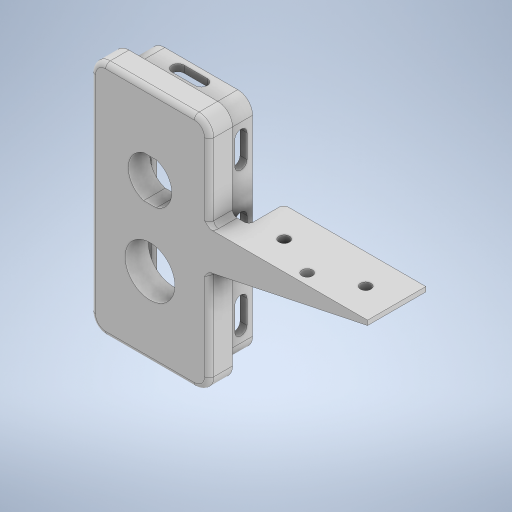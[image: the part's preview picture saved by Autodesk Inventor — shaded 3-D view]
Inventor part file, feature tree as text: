
AUTODESK INVENTOR PART (.ipt)
format: ipt  version: 2023 (Build 270158000, 158)  size: 452,096 bytes
history: native  units: mm
features: extrude x10, sketch x9, fillet x2, chamfer x1
ambient origin geometry x8: Origin, YZ Plane, XZ Plane, XY Plane, X Axis, Y Axis, Z Axis, Center Point
bodies: Solid1 (feature_tree)
feature tree (22):
  extrude  "Extrusion1"  Depth=50.8mm
  fillet  "Fillet1"  Radius=6.35mm
  sketch  "Sketch3"  dims[d6=3.375mm d7=6.35mm]
  sketch  "Sketch2"  dims[d3=10.0mm d4=0.0mm d5=2.0mm]
  sketch  "Sketch4"  dims[d8=21.355mm d9=33.866667mm]
  extrude  "Extrusion2"  Depth=2.0mm
  extrude  "Extrusion3"  Depth=6.35mm
  extrude  "Extrusion4"  Depth=33.866667mm
  extrude  "Extrusion5"  Depth=18.65mm
  chamfer  "Chamfer1"  Distance=12.0mm
  extrude  "Extrusion6"  Depth=2.0mm
  extrude  "Extrusion7"  Depth=10.0mm TaperAngle=0.0deg
  extrude  "Extrusion8"  Depth=2.0mm
  sketch  "Sketch9"  dims[d18=3.0mm d19=0.0mm d20=27.6mm d21=10.0mm d22=0.0mm d23=21.75mm d24=0.75mm d25=0.0mm d26=3.0mm d27=2.0mm d28=45.0deg d29=2.613mm d30=7.0mm d31=2.613mm d32=20.0mm d33=20.0mm d34=2.613mm d35=10.0mm d36=0.0mm d37=0.0mm d38=2.613mm d39=10.0mm d40=7.0mm d41=0.0mm d42=0.0mm d43=2.0mm d44=17.5mm d45=68.0mm d46=62.4mm d47=10.0mm d48=0.0mm d49=4.5mm d50=7.6mm d51=35.0mm d52=13.0mm d53=7.0mm d54=4.6mm d55=25.0mm d56=10.0mm d57=0.0mm d58=0.0mm d59=0.0mm d60=2.0mm]
  extrude  "Extrusion9"  Depth=2.0mm TaperAngle=0.0deg
  extrude  "Extrusion10"  Depth=2.0mm TaperAngle=45.0deg
  fillet  "Fillet2"  Radius=2.613mm
  sketch  "Sketch1"  dims[d0=101.6mm d1=50.8mm d2=6.35mm]
  sketch  "Sketch5"  dims[d10=33.866667mm d11=18.65mm]
  sketch  "Sketch6"  dims[d13=17.85mm]
  sketch  "Sketch7"  dims[d14=3.0mm]
  sketch  "Sketch8"  dims[d15=3.0mm d16=12.0mm d17=0.0mm]
